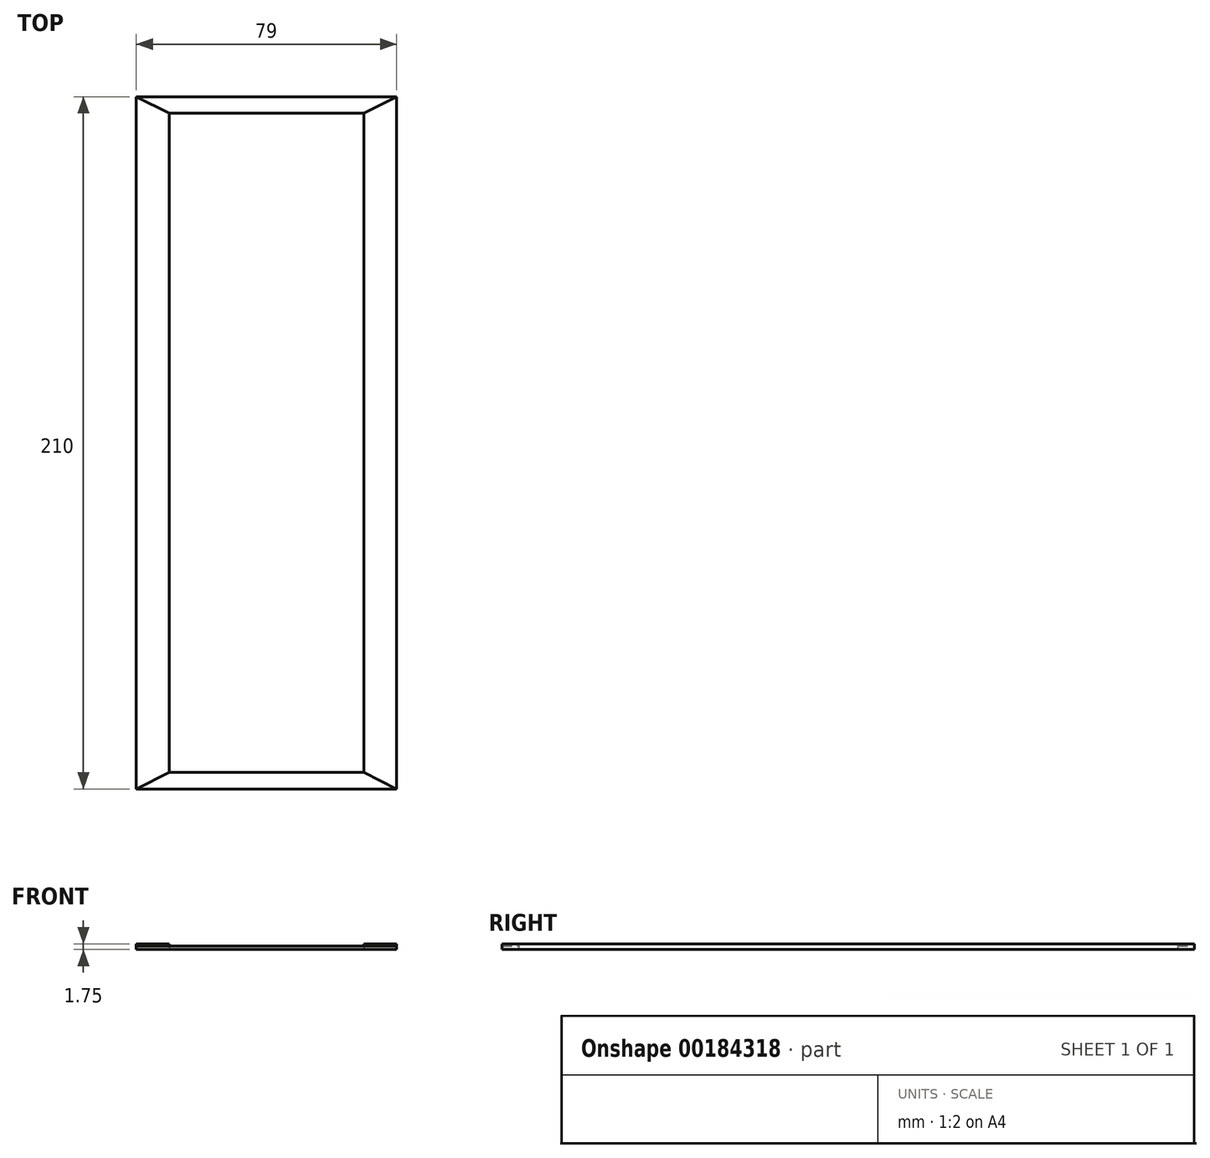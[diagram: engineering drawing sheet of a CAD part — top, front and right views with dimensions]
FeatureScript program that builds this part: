
annotation { "Feature Type Name" : "Feature", "Feature Type Description" : "" }
export const myFeature = defineFeature(function(context is Context, id is Id, definition is map)
    precondition{}
    {
        {
            var Q0;
            Q0=qCreatedBy(makeId("Top.planeOp"),FACE);
            var sketch = newSketch(context, id + "F0", { "sketchPlane" : qUnion([Q0])});
            skLineSegment(sketch, "E0.bottom", {"start": v(39.5, -105) * mm, "end": v(-39.5, -105) * mm});
            skLineSegment(sketch, "E0.top", {"start": v(39.5, 105) * mm, "end": v(-39.5, 105) * mm});
            skLineSegment(sketch, "E0.left", {"start": v(39.5, -105) * mm, "end": v(39.5, 105) * mm});
            skLineSegment(sketch, "E0.right", {"start": v(-39.5, -105) * mm, "end": v(-39.5, 105) * mm});
            skPoint(sketch, "E0.middle", {"position": v(0, 0) * mm});
            skLineSegment(sketch, "E1", {"start": v(-29.5, 105) * mm, "end": v(-29.5, -105) * mm, "construction": true});
            skLineSegment(sketch, "E2.MirrorCS", {"start": v(29.5, 105) * mm, "end": v(29.5, -105) * mm, "construction": true});
            skLineSegment(sketch, "E3", {"start": v(-29.5, 100) * mm, "end": v(-29.5, -100) * mm});
            skLineSegment(sketch, "E4", {"start": v(-29.5, -100) * mm, "end": v(29.5, -100) * mm});
            skLineSegment(sketch, "E5", {"start": v(29.5, -100) * mm, "end": v(29.5, 100) * mm});
            skLineSegment(sketch, "E6", {"start": v(29.5, 100) * mm, "end": v(-29.5, 100) * mm});
            skSolve(sketch);
        }
        {
            var Q0;
            Q0=makeQuery(id+"F0.imprint","IMPRINT",FACE,{"disambiguationData":[TD([[makeQuery(id+"F0.imprint","IMPRINT",EDGE,{"derivedFrom":sQuery(id+"F0.wireOp",EDGE,"E0.bottom")}),-1.0]])]});
            extrude(context, id + "F1", {"entities" : qUnion([Q0]), "depth" : 1 * mm});
        }
        {
            var Q0;
            Q0=makeQuery(id+"F1.opExtrude","CAP_FACE",FACE,{"disambiguationData":[OSD([sQuery(id+"F0.wireOp",EDGE,"E0.bottom"),sQuery(id+"F0.wireOp",EDGE,"E0.top"),sQuery(id+"F0.wireOp",EDGE,"E0.left"),sQuery(id+"F0.wireOp",EDGE,"E0.right"),sQuery(id+"F0.wireOp",EDGE,"E3"),sQuery(id+"F0.wireOp",EDGE,"E4"),sQuery(id+"F0.wireOp",EDGE,"E5"),sQuery(id+"F0.wireOp",EDGE,"E6")])],"isStart":false});
            var sketch = newSketch(context, id + "F2", { "sketchPlane" : qUnion([Q0])});
            skLineSegment(sketch, "E7", {"start": v(-39.5, 105) * mm, "end": v(-29.5, 100) * mm});
            skLineSegment(sketch, "E8", {"start": v(-29.5, 100) * mm, "end": v(-29.5, -100) * mm});
            skLineSegment(sketch, "E9", {"start": v(-29.5, -100) * mm, "end": v(-39.5, -105) * mm});
            skLineSegment(sketch, "E10", {"start": v(-39.5, -105) * mm, "end": v(-39.5, 105) * mm});
            skLineSegment(sketch, "E11", {"start": v(29.5, 100) * mm, "end": v(39.5, 105) * mm});
            skLineSegment(sketch, "E12", {"start": v(39.5, 105) * mm, "end": v(39.5, -105) * mm});
            skLineSegment(sketch, "E13", {"start": v(39.5, -105) * mm, "end": v(29.5, -100) * mm});
            skLineSegment(sketch, "E14", {"start": v(29.5, -100) * mm, "end": v(29.5, 100) * mm});
            skSolve(sketch);
        }
        {
            var Q0;
            Q0=makeQuery(id+"F2.imprint","IMPRINT",FACE,{"disambiguationData":[TD([[makeQuery(id+"F2.imprint","IMPRINT",EDGE,{"derivedFrom":sQuery(id+"F2.wireOp",EDGE,"E7")}),-1.0]])]});
            var Q1;
            Q1=makeQuery(id+"F2.imprint","IMPRINT",FACE,{"disambiguationData":[TD([[makeQuery(id+"F2.imprint","IMPRINT",EDGE,{"derivedFrom":sQuery(id+"F2.wireOp",EDGE,"E11")}),-1.0]])]});
            extrude(context, id + "F3", {"entities" : qUnion([Q0, Q1]), "operationType" : NewBodyOperationType.ADD, "depth" : .75 * mm});
        }
    });
